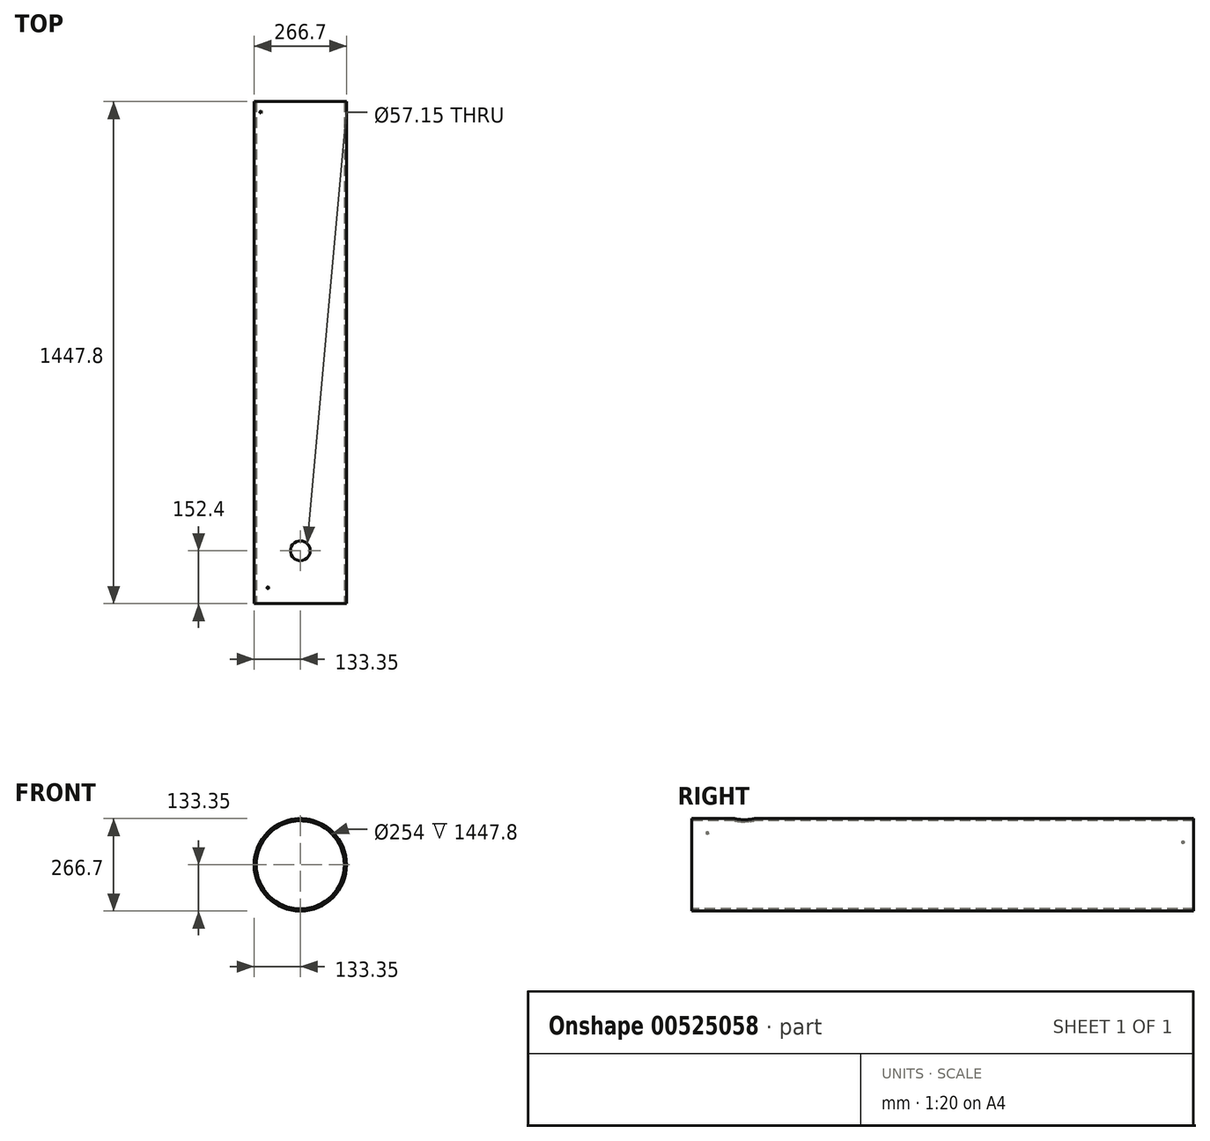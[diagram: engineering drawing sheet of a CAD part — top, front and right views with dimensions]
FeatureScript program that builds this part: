
annotation { "Feature Type Name" : "Feature", "Feature Type Description" : "" }
export const myFeature = defineFeature(function(context is Context, id is Id, definition is map)
    precondition{}
    {
        {
            var Q0;
            Q0=qCreatedBy(makeId("Front.planeOp"),FACE);
            var sketch = newSketch(context, id + "F0", { "sketchPlane" : qUnion([Q0])});
            skCircle(sketch, "E0", {"center": v(0, 0) * mm, "radius": 127 * mm});
            skCircle(sketch, "E1", {"center": v(0, 0) * mm, "radius": 133.35 * mm});
            skPoint(sketch, "E2", {"position": v(0, 133.35) * mm});
            skLineSegment(sketch, "E3", {"start": v(0, 0) * mm, "end": v(0, 133.35) * mm, "construction": true});
            skLineSegment(sketch, "E4", {"start": v(0, 0) * mm, "end": v(-94.3, 94.3) * mm, "construction": true});
            skLineSegment(sketch, "E5", {"start": v(0, 0) * mm, "end": v(-115.48, 66.67) * mm, "construction": true});
            skSolve(sketch);
        }
        {
            var Q0;
            Q0=qCreatedBy(makeId("Top.planeOp"),FACE);
            var sketch = newSketch(context, id + "F1", { "sketchPlane" : qUnion([Q0])});
            skLineSegment(sketch, "E6", {"start": v(0, 0) * mm, "end": v(0, -103.92) * mm, "construction": true});
            skSolve(sketch);
        }
        {
            var Q0;
            Q0 = qSketchRegion(id + "F0", true);
            extrude(context, id + "F2", {"entities" : qUnion([Q0]), "oppositeDirection" : true, "depth" : 1447.8 * mm, "offsetDistance" : 25.4 * mm});
        }
        {
            var Q0;
            Q0=qCreatedBy(makeId("Top.planeOp"),FACE);
            var Q1;
            Q1=sQuery(id+"F0.wireOp",VERTEX,"E2");
            cPlane(context, id + "F3", {"entities" : qUnion([Q0, Q1]), "cplaneType" : CPlaneType.PLANE_POINT, "offset" : 25.4 * mm, "width" : 152.4 * mm, "height" : 152.4 * mm});
        }
        {
            var Q0;
            Q0=qCreatedBy(id+"F3.planeOp",FACE);
            var sketch = newSketch(context, id + "F4", { "sketchPlane" : qUnion([Q0])});
            skPoint(sketch, "E7", {"position": v(0, 152.4) * mm});
            skLineSegment(sketch, "E8", {"start": v(0, 0) * mm, "end": v(0, 76.65) * mm, "construction": true});
            skSolve(sketch);
        }
        {
            var Q0;
            Q0=sQuery(id+"F4.wireOp",VERTEX,"E7");
            var Q1;
            Q1=makeQuery(id+"F2.opExtrude","SWEPT_BODY",BODY,{"disambiguationData":[OSD([sQuery(id+"F0.wireOp",EDGE,"E0"),sQuery(id+"F0.wireOp",EDGE,"E1")])]});
            hole(context, id + "F5", {"style" : HoleStyle.SIMPLE, "endStyle" : HoleEndStyle.BLIND, "holeDiameter" : 57.15 * mm, "holeDepth" : 12.7 * mm, "isTappedThrough" : true, "tappedDepth" : 12.7 * mm, "tapClearance" : 3, "locations" : qUnion([Q0]), "scope" : qUnion([Q1])});
        }
        {
            var Q0;
            Q0=sQuery(id+"F0.wireOp",VERTEX,"E4.end");
            var Q1;
            Q1=sQuery(id+"F0.wireOp",EDGE,"E4");
            cPlane(context, id + "F6", {"entities" : qUnion([Q0, Q1]), "cplaneType" : CPlaneType.LINE_POINT, "offset" : 25.4 * mm, "width" : 152.4 * mm, "height" : 152.4 * mm});
        }
        {
            var Q0;
            Q0=qCreatedBy(id+"F6.planeOp",FACE);
            var sketch = newSketch(context, id + "F7", { "sketchPlane" : qUnion([Q0])});
            skCircle(sketch, "E9", {"center": v(-45.72, 0) * mm, "radius": 2.38 * mm});
            skSolve(sketch);
        }
        {
            var Q0;
            Q0 = qSketchRegion(id + "F7", true);
            extrude(context, id + "F8", {"entities" : qUnion([Q0]), "operationType" : NewBodyOperationType.REMOVE, "oppositeDirection" : true, "depth" : 25.4 * mm, "offsetDistance" : 25.4 * mm});
        }
        {
            var Q0;
            Q0=sQuery(id+"F0.wireOp",VERTEX,"E5.end");
            var Q1;
            Q1=sQuery(id+"F0.wireOp",EDGE,"E5");
            cPlane(context, id + "F9", {"entities" : qUnion([Q0, Q1]), "cplaneType" : CPlaneType.LINE_POINT, "offset" : 25.4 * mm, "width" : 152.4 * mm, "height" : 152.4 * mm});
        }
        {
            var Q0;
            Q0=qCreatedBy(id+"F9.planeOp",FACE);
            var sketch = newSketch(context, id + "F10", { "sketchPlane" : qUnion([Q0])});
            skCircle(sketch, "E10", {"center": v(-1417.45, 0) * mm, "radius": 2.38 * mm});
            skSolve(sketch);
        }
        {
            var Q0;
            Q0 = qSketchRegion(id + "F10", true);
            extrude(context, id + "F11", {"entities" : qUnion([Q0]), "operationType" : NewBodyOperationType.REMOVE, "oppositeDirection" : true, "depth" : 25.4 * mm, "offsetDistance" : 25.4 * mm});
        }
    });
